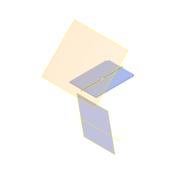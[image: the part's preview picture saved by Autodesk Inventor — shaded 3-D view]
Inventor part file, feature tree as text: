
AUTODESK INVENTOR PART (.ipt)
format: ipt  version: 2019.4 (Build 234330000, 330)  size: 117,760 bytes
history: native  units: in
note: dims shown in document units (in); Inventor stores cm internally (conversion verified against a paired STEP export)
features: other x5, plane x4, extrude x3, sketch x3
ambient origin geometry x8: Origin, YZ Plane, XZ Plane, XY Plane, X Axis, Y Axis, Z Axis, Center Point
bodies: Solid1 (feature_tree)
feature tree (15):
  extrude  "Extrusion1"  Depth=0.0127in
  plane  "Work Plane1"
  extrude  "Extrusion2"  Depth=0.9843in
  plane  "Work Plane2"
  plane  "Work Plane3"
  plane  "Work Plane4"
  extrude  "Extrusion3"  Depth=0.3937in TaperAngle=0.0deg
  sketch  "Sketch1"  dims[d2=0.0394in d3=0.0in d4=0.0127in]
  sketch  "Sketch2"  dims[d5=0.0079in d6=0.0in d7=0.9843in]
  sketch  "Sketch3"  dims[d8=1.4173in d9=0.3937in d10=0.0in]
  other  "Assembly_Cube_Dichroic_Beamsplitter.iam"
  other  "Assembly_Cube_empty_1x1_v2:1"
  other  "10_Cube_1x1_v2:1"
  other  "Assembly_Cube_Dichroic_Beamsplitter_multi_motorized_revolver_25x35_v3.iam"
  other  "10_Cube_1x1_IM:3"
